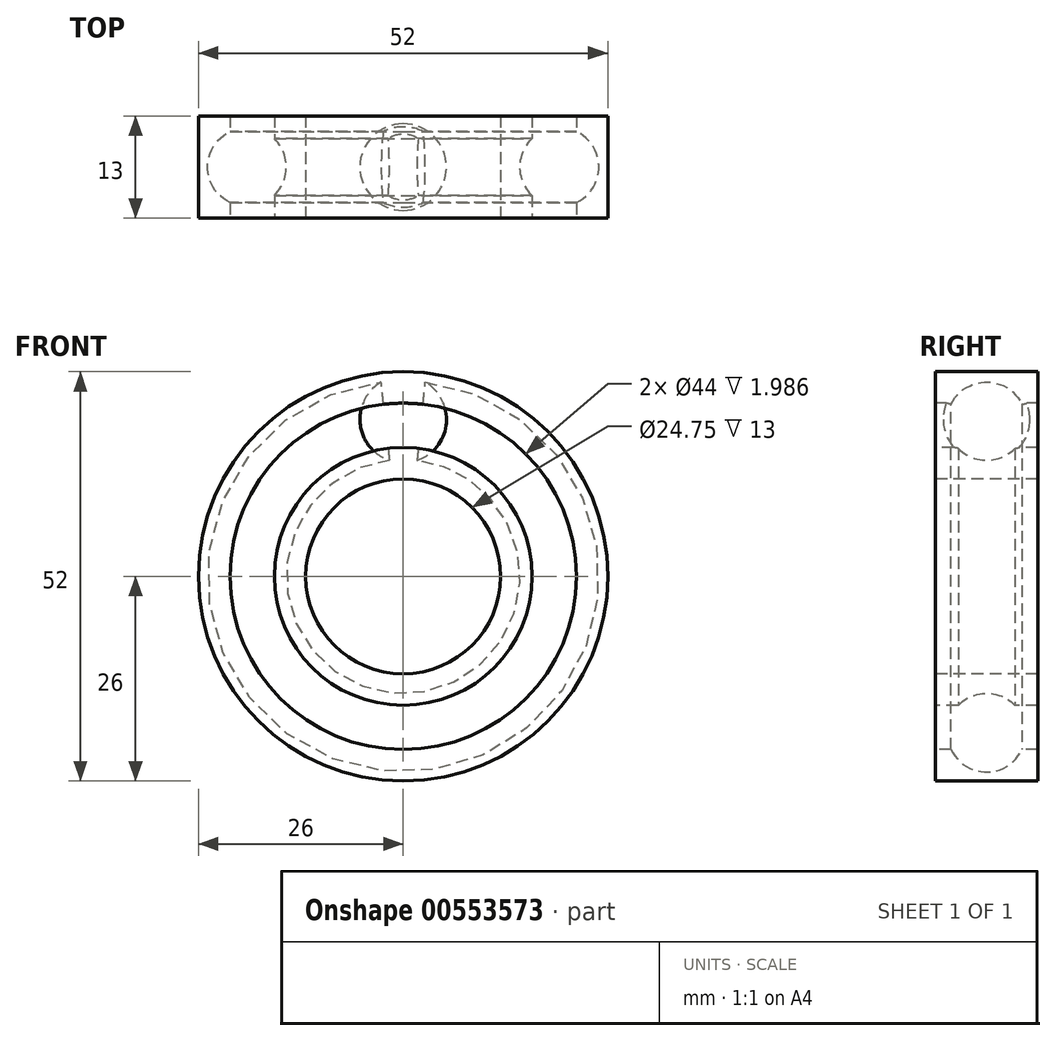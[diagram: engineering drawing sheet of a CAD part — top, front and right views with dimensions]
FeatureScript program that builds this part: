
annotation { "Feature Type Name" : "Feature", "Feature Type Description" : "" }
export const myFeature = defineFeature(function(context is Context, id is Id, definition is map)
    precondition{}
    {
        {
            var Q0;
            Q0=qCreatedBy(makeId("Right.planeOp"),FACE);
            var sketch = newSketch(context, id + "F0", { "sketchPlane" : qUnion([Q0])});
            skLineSegment(sketch, "E0.bottom", {"start": v(6.5, 26) * mm, "end": v(-6.5, 26) * mm});
            skLineSegment(sketch, "E0.top", {"start": v(6.5, 22) * mm, "end": v(4.51, 22) * mm});
            skLineSegment(sketch, "E0.left", {"start": v(6.5, 26) * mm, "end": v(6.5, 22) * mm});
            skLineSegment(sketch, "E0.right", {"start": v(-6.5, 26) * mm, "end": v(-6.5, 22) * mm});
            skPoint(sketch, "E0.middle", {"position": v(0, 24) * mm});
            skLineSegment(sketch, "E1.bottom", {"start": v(6.5, 16.37) * mm, "end": v(3.6, 16.37) * mm});
            skLineSegment(sketch, "E1.top", {"start": v(6.5, 12.38) * mm, "end": v(-6.5, 12.38) * mm});
            skLineSegment(sketch, "E1.left", {"start": v(6.5, 16.37) * mm, "end": v(6.5, 12.38) * mm});
            skLineSegment(sketch, "E1.right", {"start": v(-6.5, 16.37) * mm, "end": v(-6.5, 12.38) * mm});
            skPoint(sketch, "E1.middle", {"position": v(0, 14.37) * mm});
            skArc(sketch, "E2", {"start": v(-3.6, 16.37) * mm, "mid": v(0, 14.85) * mm, "end": v(3.6, 16.37) * mm});
            skLineSegment(sketch, "E3.trimOffspring", {"start": v(-4.51, 22) * mm, "end": v(-6.5, 22) * mm});
            skLineSegment(sketch, "E4.trimOffspring", {"start": v(-3.6, 16.37) * mm, "end": v(-6.5, 16.37) * mm});
            skArc(sketch, "E5.trimOffspring", {"start": v(4.51, 22) * mm, "mid": v(0, 24.85) * mm, "end": v(-4.51, 22) * mm});
            skLineSegment(sketch, "E6", {"start": v(-52.23, 0) * mm, "end": v(41.22, 0) * mm, "construction": true});
            skSolve(sketch);
        }
        {
            var Q0;
            Q0 = qSketchRegion(id + "F0", true);
            var Q1;
            Q1=sQuery(id+"F0.wireOp",EDGE,"E6");
            revolve(context, id + "F1", {"entities" : qUnion([Q0]), "axis" : qUnion([Q1]), "revolveType" : RevolveType.FULL});
        }
        {
            var Q0;
            Q0=qCreatedBy(makeId("Right.planeOp"),FACE);
            var sketch = newSketch(context, id + "F2", { "sketchPlane" : qUnion([Q0])});
            skLineSegment(sketch, "E7.0", {"start": v(-4.51, -22) * mm, "end": v(-4.51, 22) * mm});
            skLineSegment(sketch, "E8.0", {"start": v(4.51, -22) * mm, "end": v(4.51, 22) * mm});
            skArc(sketch, "E9", {"start": v(5.5, 19.96) * mm, "mid": v(0, 25.46) * mm, "end": v(-5.5, 19.96) * mm});
            skLineSegment(sketch, "E10", {"start": v(-5.5, 19.96) * mm, "end": v(5.5, 19.96) * mm});
            skSolve(sketch);
        }
        {
            var Q0;
            Q0 = qSketchRegion(id + "F2", true);
            var Q1;
            Q1=sQuery(id+"F2.wireOp",EDGE,"E10");
            revolve(context, id + "F3", {"operationType" : NewBodyOperationType.ADD, "entities" : qUnion([Q0]), "axis" : qUnion([Q1]), "revolveType" : RevolveType.FULL});
        }
    });
